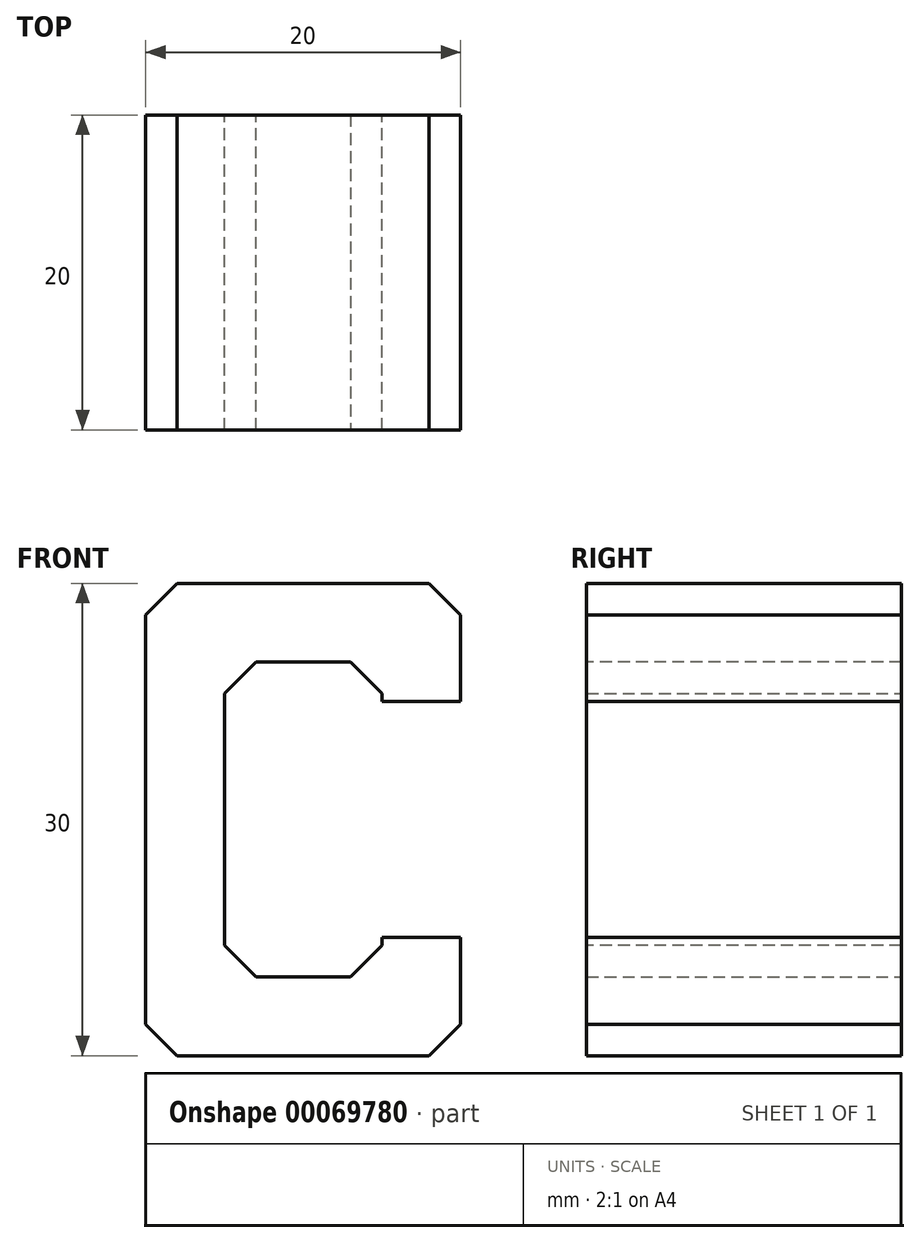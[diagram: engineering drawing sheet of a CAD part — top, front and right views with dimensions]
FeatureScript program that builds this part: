
annotation { "Feature Type Name" : "Feature", "Feature Type Description" : "" }
export const myFeature = defineFeature(function(context is Context, id is Id, definition is map)
    precondition{}
    {
        {
            var Q0;
            Q0=qCreatedBy(makeId("Front.planeOp"),FACE);
            var sketch = newSketch(context, id + "F0", { "sketchPlane" : qUnion([Q0])});
            skLineSegment(sketch, "E0.bottom", {"start": v(0, 0) * mm, "end": v(20, 0) * mm});
            skLineSegment(sketch, "E0.top", {"start": v(0, 30) * mm, "end": v(20, 30) * mm});
            skLineSegment(sketch, "E0.left", {"start": v(0, 0) * mm, "end": v(0, 30) * mm});
            skLineSegment(sketch, "E0.right", {"start": v(20, 0) * mm, "end": v(20, 7.5) * mm});
            skLineSegment(sketch, "E1", {"start": v(15, 25) * mm, "end": v(5, 25) * mm});
            skLineSegment(sketch, "E2", {"start": v(5, 5) * mm, "end": v(15, 5) * mm});
            skLineSegment(sketch, "E3", {"start": v(5, 25) * mm, "end": v(5, 5) * mm});
            skLineSegment(sketch, "E4", {"start": v(15, 25) * mm, "end": v(15, 22.5) * mm});
            skLineSegment(sketch, "E5", {"start": v(20, 22.5) * mm, "end": v(15, 22.5) * mm});
            skLineSegment(sketch, "E6", {"start": v(15, 7.5) * mm, "end": v(20, 7.5) * mm});
            skLineSegment(sketch, "E7.trimOffspring", {"start": v(20, 22.5) * mm, "end": v(20, 30) * mm});
            skLineSegment(sketch, "E8.trimOffspring", {"start": v(15, 7.5) * mm, "end": v(15, 5) * mm});
            skSolve(sketch);
        }
        {
            var Q0;
            Q0=makeQuery(id+"F0.imprint","IMPRINT",FACE,{"disambiguationData":[TD([[makeQuery(id+"F0.imprint","IMPRINT",EDGE,{"derivedFrom":sQuery(id+"F0.wireOp",EDGE,"E0.bottom")}),1.0]])]});
            extrude(context, id + "F1", {"entities" : qUnion([Q0]), "depth" : 20 * mm});
        }
        {
            var Q0;
            Q0=makeQuery(id+"F1.opExtrude","SWEPT_EDGE",EDGE,{"disambiguationData":[OSD([sQuery(id+"F0.wireOp",EDGE,"E0.top"),sQuery(id+"F0.wireOp",EDGE,"E7.trimOffspring")])]});
            var Q1;
            Q1=makeQuery(id+"F1.opExtrude","SWEPT_EDGE",EDGE,{"disambiguationData":[OSD([sQuery(id+"F0.wireOp",EDGE,"E0.top"),sQuery(id+"F0.wireOp",EDGE,"E0.left")])]});
            var Q2;
            Q2=makeQuery(id+"F1.opExtrude","SWEPT_EDGE",EDGE,{"disambiguationData":[OSD([sQuery(id+"F0.wireOp",EDGE,"E0.bottom"),sQuery(id+"F0.wireOp",EDGE,"E0.right")])]});
            var Q3;
            Q3=makeQuery(id+"F1.opExtrude","SWEPT_EDGE",EDGE,{"disambiguationData":[OSD([sQuery(id+"F0.wireOp",EDGE,"E0.bottom"),sQuery(id+"F0.wireOp",EDGE,"E0.left")])]});
            var Q4;
            Q4=makeQuery(id+"F1.opExtrude","SWEPT_EDGE",EDGE,{"disambiguationData":[OSD([sQuery(id+"F0.wireOp",EDGE,"E1"),sQuery(id+"F0.wireOp",EDGE,"E3")])]});
            var Q5;
            Q5=makeQuery(id+"F1.opExtrude","SWEPT_EDGE",EDGE,{"disambiguationData":[OSD([sQuery(id+"F0.wireOp",EDGE,"E2"),sQuery(id+"F0.wireOp",EDGE,"E3")])]});
            var Q6;
            Q6=makeQuery(id+"F1.opExtrude","SWEPT_EDGE",EDGE,{"disambiguationData":[OSD([sQuery(id+"F0.wireOp",EDGE,"E1"),sQuery(id+"F0.wireOp",EDGE,"E4")])]});
            var Q7;
            Q7=makeQuery(id+"F1.opExtrude","SWEPT_EDGE",EDGE,{"disambiguationData":[OSD([sQuery(id+"F0.wireOp",EDGE,"E2"),sQuery(id+"F0.wireOp",EDGE,"E8.trimOffspring")])]});
            chamfer(context, id + "F2", {"entities" : qUnion([Q0, Q1, Q2, Q3, Q4, Q5, Q6, Q7]), "width" : 2 * mm, "tangentPropagation" : true});
        }
    });
